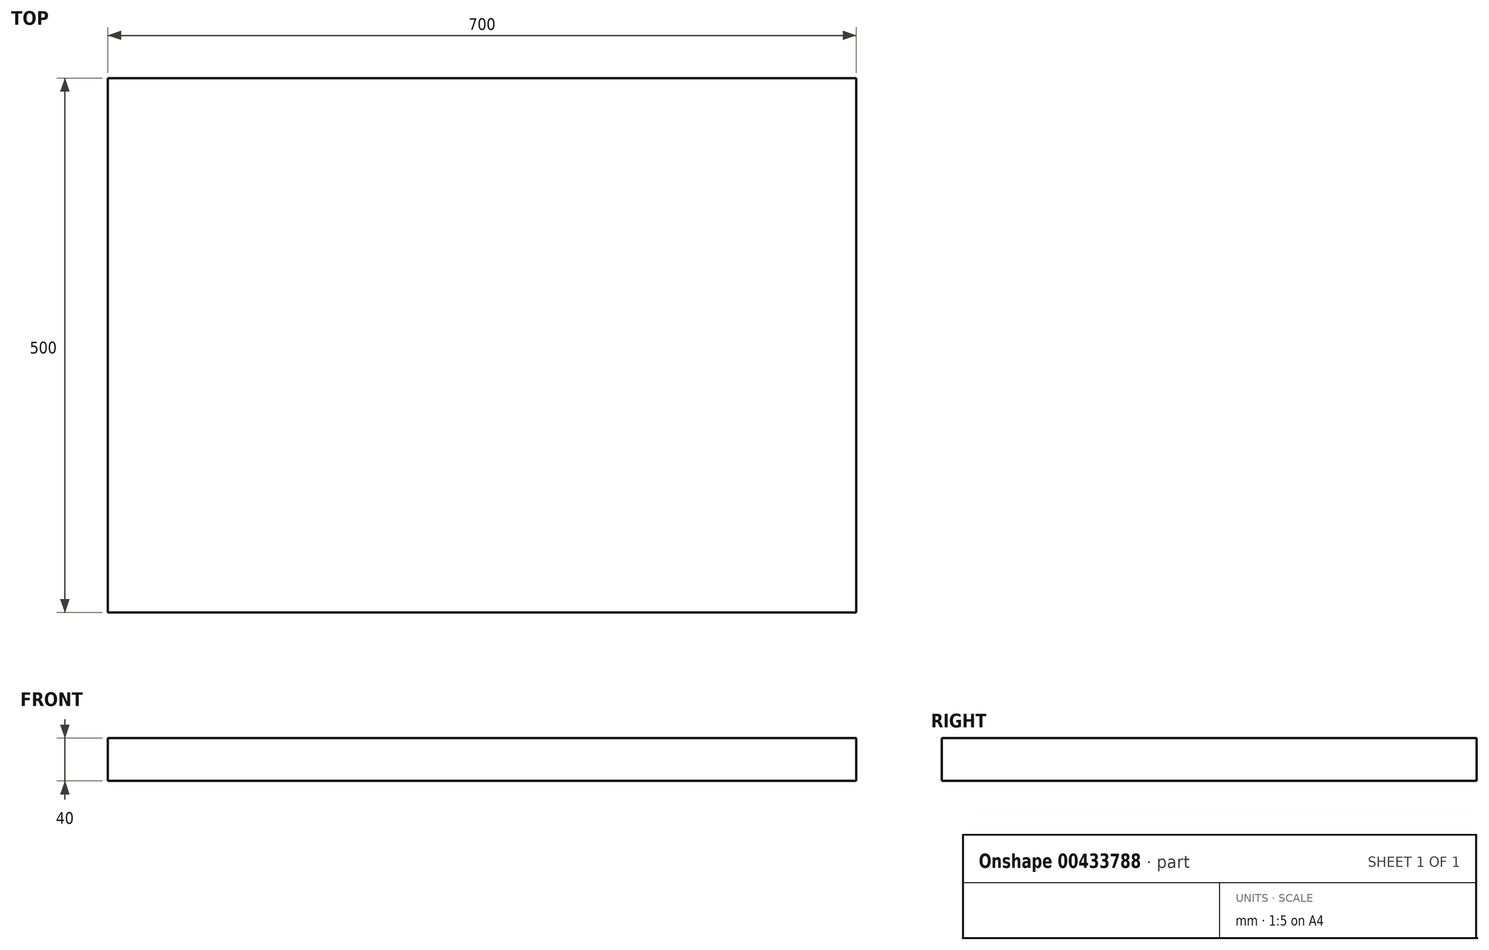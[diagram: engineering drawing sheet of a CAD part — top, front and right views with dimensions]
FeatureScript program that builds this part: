
annotation { "Feature Type Name" : "Feature", "Feature Type Description" : "" }
export const myFeature = defineFeature(function(context is Context, id is Id, definition is map)
    precondition{}
    {
        {
            var Q0;
            Q0=qCreatedBy(makeId("Top.planeOp"),FACE);
            var sketch = newSketch(context, id + "F0", { "sketchPlane" : qUnion([Q0])});
            skLineSegment(sketch, "E0.bottom", {"start": v(0, 0) * mm, "end": v(700, 0) * mm});
            skLineSegment(sketch, "E0.top", {"start": v(0, 500) * mm, "end": v(700, 500) * mm});
            skLineSegment(sketch, "E0.left", {"start": v(0, 0) * mm, "end": v(0, 500) * mm});
            skLineSegment(sketch, "E0.right", {"start": v(700, 0) * mm, "end": v(700, 500) * mm});
            skSolve(sketch);
        }
        {
            var Q0;
            Q0=makeQuery(id+"F0.imprint","IMPRINT",FACE,{"disambiguationData":[TD([[makeQuery(id+"F0.imprint","IMPRINT",EDGE,{"derivedFrom":sQuery(id+"F0.wireOp",EDGE,"E0.bottom")}),1.0]])]});
            extrude(context, id + "F1", {"entities" : qUnion([Q0]), "depth" : 40 * mm});
        }
    });
